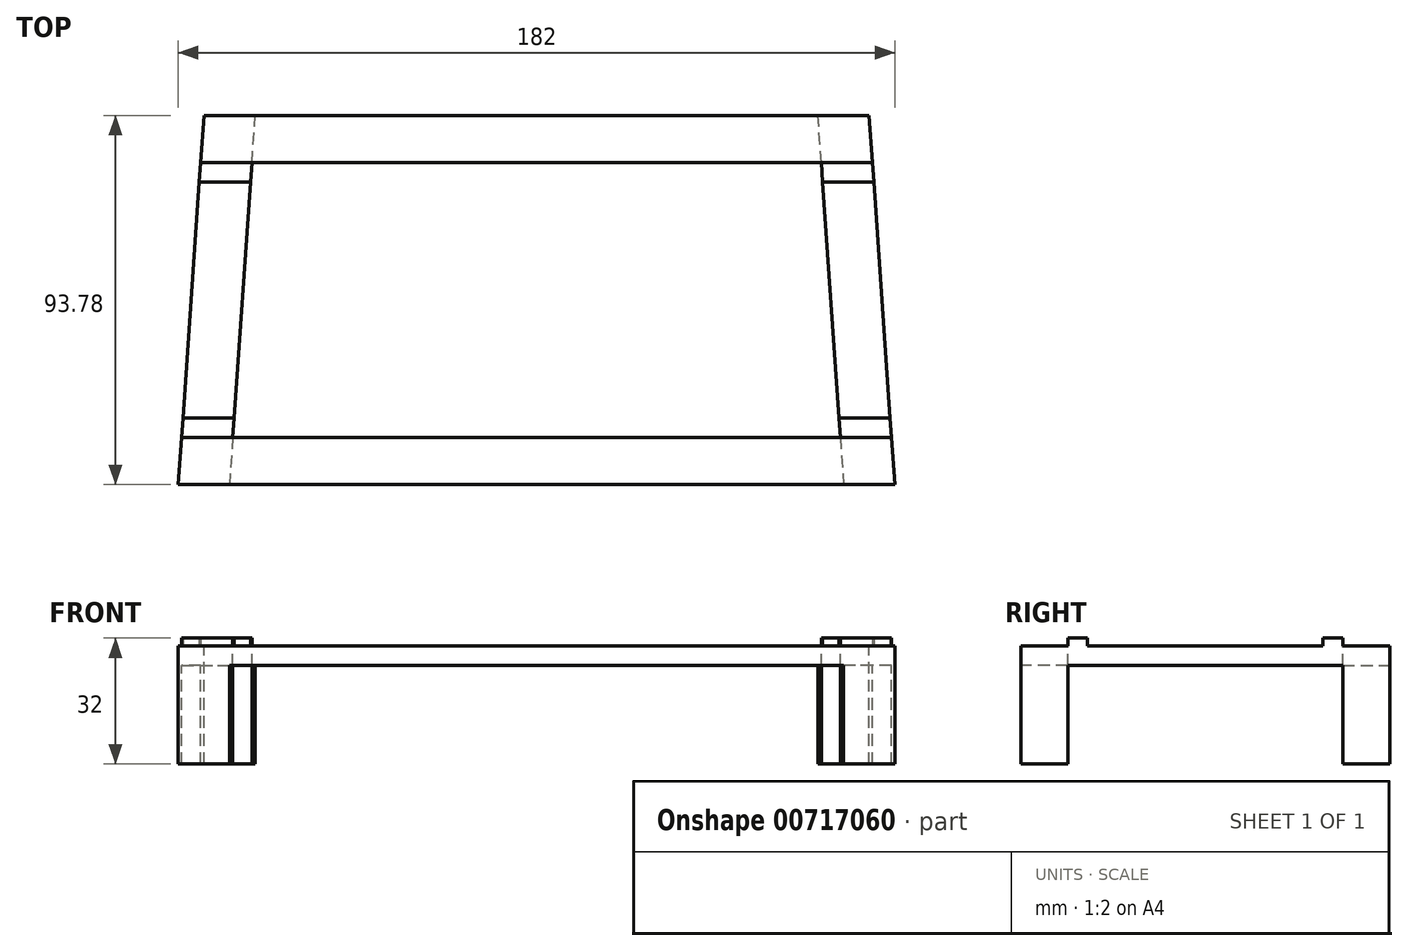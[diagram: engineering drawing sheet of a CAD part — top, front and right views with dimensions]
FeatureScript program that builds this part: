
annotation { "Feature Type Name" : "Feature", "Feature Type Description" : "" }
export const myFeature = defineFeature(function(context is Context, id is Id, definition is map)
    precondition{}
    {
        {
            var Q0;
            Q0=qCreatedBy(makeId("Top.planeOp"),FACE);
            var sketch = newSketch(context, id + "F0", { "sketchPlane" : qUnion([Q0])});
            skLineSegment(sketch, "E0", {"start": v(-91, -46.89) * mm, "end": v(91, -46.89) * mm});
            skLineSegment(sketch, "E1", {"start": v(91, -46.89) * mm, "end": v(84.5, 46.89) * mm});
            skLineSegment(sketch, "E2", {"start": v(84.5, 46.89) * mm, "end": v(-84.5, 46.89) * mm});
            skLineSegment(sketch, "E3", {"start": v(-84.5, 46.89) * mm, "end": v(-91, -46.89) * mm});
            skLineSegment(sketch, "E4", {"start": v(0, 46.89) * mm, "end": v(0, 0) * mm, "construction": true});
            skLineSegment(sketch, "E5", {"start": v(-87.75, 0) * mm, "end": v(0, 0) * mm, "construction": true});
            skLineSegment(sketch, "E6", {"start": v(0, 0) * mm, "end": v(87.75, 0) * mm, "construction": true});
            skLineSegment(sketch, "E7", {"start": v(0, 0) * mm, "end": v(0, -46.89) * mm, "construction": true});
            skLineSegment(sketch, "E8", {"start": v(85.33, 34.92) * mm, "end": v(72.33, 34.92) * mm});
            skLineSegment(sketch, "E9", {"start": v(72.33, 34.92) * mm, "end": v(71.5, 46.89) * mm});
            skLineSegment(sketch, "E10", {"start": v(-85.33, 34.92) * mm, "end": v(-72.33, 34.92) * mm});
            skLineSegment(sketch, "E11", {"start": v(-72.33, 34.92) * mm, "end": v(-71.5, 46.89) * mm});
            skLineSegment(sketch, "E12", {"start": v(90.17, -34.92) * mm, "end": v(77.17, -34.92) * mm});
            skLineSegment(sketch, "E13", {"start": v(77.17, -34.92) * mm, "end": v(78, -46.89) * mm});
            skLineSegment(sketch, "E14", {"start": v(-90.17, -34.92) * mm, "end": v(-77.17, -34.92) * mm});
            skLineSegment(sketch, "E15", {"start": v(-77.17, -34.92) * mm, "end": v(-78, -46.89) * mm});
            skLineSegment(sketch, "E16.0", {"start": v(-71.81, -29.92) * mm, "end": v(-72.99, -46.89) * mm});
            skLineSegment(sketch, "E16.1", {"start": v(-89.82, -29.92) * mm, "end": v(-71.81, -29.92) * mm});
            skLineSegment(sketch, "E17.0", {"start": v(71.81, -29.92) * mm, "end": v(72.99, -46.89) * mm});
            skLineSegment(sketch, "E17.1", {"start": v(89.82, -29.92) * mm, "end": v(71.81, -29.92) * mm});
            skLineSegment(sketch, "E18.0", {"start": v(67.66, 29.92) * mm, "end": v(66.49, 46.89) * mm});
            skLineSegment(sketch, "E18.1", {"start": v(85.68, 29.92) * mm, "end": v(67.66, 29.92) * mm});
            skLineSegment(sketch, "E19.0", {"start": v(-67.66, 29.92) * mm, "end": v(-66.49, 46.89) * mm});
            skLineSegment(sketch, "E19.1", {"start": v(-85.68, 29.92) * mm, "end": v(-67.66, 29.92) * mm});
            skLineSegment(sketch, "E20", {"start": v(-72.33, 34.92) * mm, "end": v(-77.17, -34.92) * mm});
            skLineSegment(sketch, "E21", {"start": v(77.17, -34.92) * mm, "end": v(-77.17, -34.92) * mm});
            skLineSegment(sketch, "E22", {"start": v(72.33, 34.92) * mm, "end": v(77.17, -34.92) * mm});
            skLineSegment(sketch, "E23", {"start": v(72.33, 34.92) * mm, "end": v(-72.33, 34.92) * mm});
            skSolve(sketch);
        }
        {
            var Q0;
            {var subQ4=sQuery(id+"F0.wireOp",EDGE,"E10");Q0=makeQuery(id+"F0.imprint","IMPRINT",FACE,{"disambiguationData":[TD([[makeQuery(id+"F0.imprint","IMPRINT",EDGE,{"derivedFrom":subQ4}),1.0]])]});}
            var Q1;
            {var subQ3=sQuery(id+"F0.wireOp",EDGE,"E8");Q1=makeQuery(id+"F0.imprint","IMPRINT",FACE,{"disambiguationData":[TD([[makeQuery(id+"F0.imprint","IMPRINT",EDGE,{"derivedFrom":subQ3}),-1.0]])]});}
            var Q2;
            {var subQ4=sQuery(id+"F0.wireOp",EDGE,"E12");Q2=makeQuery(id+"F0.imprint","IMPRINT",FACE,{"disambiguationData":[TD([[makeQuery(id+"F0.imprint","IMPRINT",EDGE,{"derivedFrom":subQ4}),1.0]])]});}
            var Q3;
            {var subQ4=sQuery(id+"F0.wireOp",EDGE,"E14");Q3=makeQuery(id+"F0.imprint","IMPRINT",FACE,{"disambiguationData":[TD([[makeQuery(id+"F0.imprint","IMPRINT",EDGE,{"derivedFrom":subQ4}),-1.0]])]});}
            extrude(context, id + "F1", {"entities" : qUnion([Q0, Q1, Q2, Q3]), "oppositeDirection" : true, "depth" : 30 * mm, "offsetDistance" : 25 * mm});
        }
        {
            var Q0;
            {var subQ0=sQuery(id+"F0.wireOp",EDGE,"E16.1");var subQ1=sQuery(id+"F0.wireOp",EDGE,"E3");var subQ2=makeQuery(id+"F0.imprint","INTERSECT",VERTEX,{"derivedFrom":[subQ1,subQ0]});Q0=makeQuery(id+"F0.imprint","IMPRINT",FACE,{"disambiguationData":[TD([[makeQuery(id+"F0.imprint","IMPRINT",EDGE,{"disambiguationData":[TD([[subQ2,1.0]])],"derivedFrom":subQ1}),1.0]])]});}
            var Q1;
            {var subQ0=sQuery(id+"F0.wireOp",EDGE,"E10");Q1=makeQuery(id+"F0.imprint","IMPRINT",FACE,{"disambiguationData":[TD([[makeQuery(id+"F0.imprint","IMPRINT",EDGE,{"derivedFrom":subQ0}),-1.0]])]});}
            var Q2;
            {var subQ0=sQuery(id+"F0.wireOp",EDGE,"E14");Q2=makeQuery(id+"F0.imprint","IMPRINT",FACE,{"disambiguationData":[TD([[makeQuery(id+"F0.imprint","IMPRINT",EDGE,{"derivedFrom":subQ0}),1.0]])]});}
            var Q3;
            {var subQ0=sQuery(id+"F0.wireOp",EDGE,"E15");Q3=makeQuery(id+"F0.imprint","IMPRINT",FACE,{"disambiguationData":[TD([[makeQuery(id+"F0.imprint","IMPRINT",EDGE,{"derivedFrom":subQ0}),1.0]])]});}
            var Q4;
            {var subQ0=sQuery(id+"F0.wireOp",EDGE,"E16.0");var subQ1=sQuery(id+"F0.wireOp",EDGE,"E0");var subQ2=makeQuery(id+"F0.imprint","INTERSECT",VERTEX,{"derivedFrom":[subQ1,subQ0]});Q4=makeQuery(id+"F0.imprint","IMPRINT",FACE,{"disambiguationData":[TD([[makeQuery(id+"F0.imprint","IMPRINT",EDGE,{"disambiguationData":[TD([[subQ2,-1.0]])],"derivedFrom":subQ1}),1.0]])]});}
            var Q5;
            {var subQ0=sQuery(id+"F0.wireOp",EDGE,"E13");Q5=makeQuery(id+"F0.imprint","IMPRINT",FACE,{"disambiguationData":[TD([[makeQuery(id+"F0.imprint","IMPRINT",EDGE,{"derivedFrom":subQ0}),-1.0]])]});}
            var Q6;
            {var subQ0=sQuery(id+"F0.wireOp",EDGE,"E12");Q6=makeQuery(id+"F0.imprint","IMPRINT",FACE,{"disambiguationData":[TD([[makeQuery(id+"F0.imprint","IMPRINT",EDGE,{"derivedFrom":subQ0}),-1.0]])]});}
            var Q7;
            {var subQ0=sQuery(id+"F0.wireOp",EDGE,"E17.1");var subQ1=sQuery(id+"F0.wireOp",EDGE,"E1");var subQ2=makeQuery(id+"F0.imprint","INTERSECT",VERTEX,{"derivedFrom":[subQ1,subQ0]});Q7=makeQuery(id+"F0.imprint","IMPRINT",FACE,{"disambiguationData":[TD([[makeQuery(id+"F0.imprint","IMPRINT",EDGE,{"disambiguationData":[TD([[subQ2,-1.0]])],"derivedFrom":subQ1}),1.0]])]});}
            var Q8;
            {var subQ0=sQuery(id+"F0.wireOp",EDGE,"E8");Q8=makeQuery(id+"F0.imprint","IMPRINT",FACE,{"disambiguationData":[TD([[makeQuery(id+"F0.imprint","IMPRINT",EDGE,{"derivedFrom":subQ0}),1.0]])]});}
            var Q9;
            {var subQ0=sQuery(id+"F0.wireOp",EDGE,"E9");Q9=makeQuery(id+"F0.imprint","IMPRINT",FACE,{"disambiguationData":[TD([[makeQuery(id+"F0.imprint","IMPRINT",EDGE,{"derivedFrom":subQ0}),1.0]])]});}
            var Q10;
            {var subQ0=sQuery(id+"F0.wireOp",EDGE,"E18.0");var subQ1=sQuery(id+"F0.wireOp",EDGE,"E2");var subQ2=makeQuery(id+"F0.imprint","INTERSECT",VERTEX,{"derivedFrom":[subQ1,subQ0]});Q10=makeQuery(id+"F0.imprint","IMPRINT",FACE,{"disambiguationData":[TD([[makeQuery(id+"F0.imprint","IMPRINT",EDGE,{"disambiguationData":[TD([[subQ2,-1.0]])],"derivedFrom":subQ1}),1.0]])]});}
            var Q11;
            {var subQ0=sQuery(id+"F0.wireOp",EDGE,"E11");Q11=makeQuery(id+"F0.imprint","IMPRINT",FACE,{"disambiguationData":[TD([[makeQuery(id+"F0.imprint","IMPRINT",EDGE,{"derivedFrom":subQ0}),-1.0]])]});}
            extrude(context, id + "F2", {"entities" : qUnion([Q0, Q1, Q2, Q3, Q4, Q5, Q6, Q7, Q8, Q9, Q10, Q11]), "operationType" : NewBodyOperationType.ADD, "oppositeDirection" : true, "depth" : 5 * mm, "offsetDistance" : 25 * mm});
        }
        {
            var Q0;
            {var subQ0=sQuery(id+"F0.wireOp",EDGE,"E10");Q0=makeQuery(id+"F0.imprint","IMPRINT",FACE,{"disambiguationData":[TD([[makeQuery(id+"F0.imprint","IMPRINT",EDGE,{"derivedFrom":subQ0}),-1.0]])]});}
            var Q1;
            {var subQ0=sQuery(id+"F0.wireOp",EDGE,"E14");Q1=makeQuery(id+"F0.imprint","IMPRINT",FACE,{"disambiguationData":[TD([[makeQuery(id+"F0.imprint","IMPRINT",EDGE,{"derivedFrom":subQ0}),1.0]])]});}
            var Q2;
            {var subQ0=sQuery(id+"F0.wireOp",EDGE,"E8");Q2=makeQuery(id+"F0.imprint","IMPRINT",FACE,{"disambiguationData":[TD([[makeQuery(id+"F0.imprint","IMPRINT",EDGE,{"derivedFrom":subQ0}),1.0]])]});}
            var Q3;
            {var subQ0=sQuery(id+"F0.wireOp",EDGE,"E12");Q3=makeQuery(id+"F0.imprint","IMPRINT",FACE,{"disambiguationData":[TD([[makeQuery(id+"F0.imprint","IMPRINT",EDGE,{"derivedFrom":subQ0}),-1.0]])]});}
            extrude(context, id + "F3", {"entities" : qUnion([Q0, Q1, Q2, Q3]), "operationType" : NewBodyOperationType.ADD, "depth" : 2 * mm, "offsetDistance" : 25 * mm});
        }
    });
